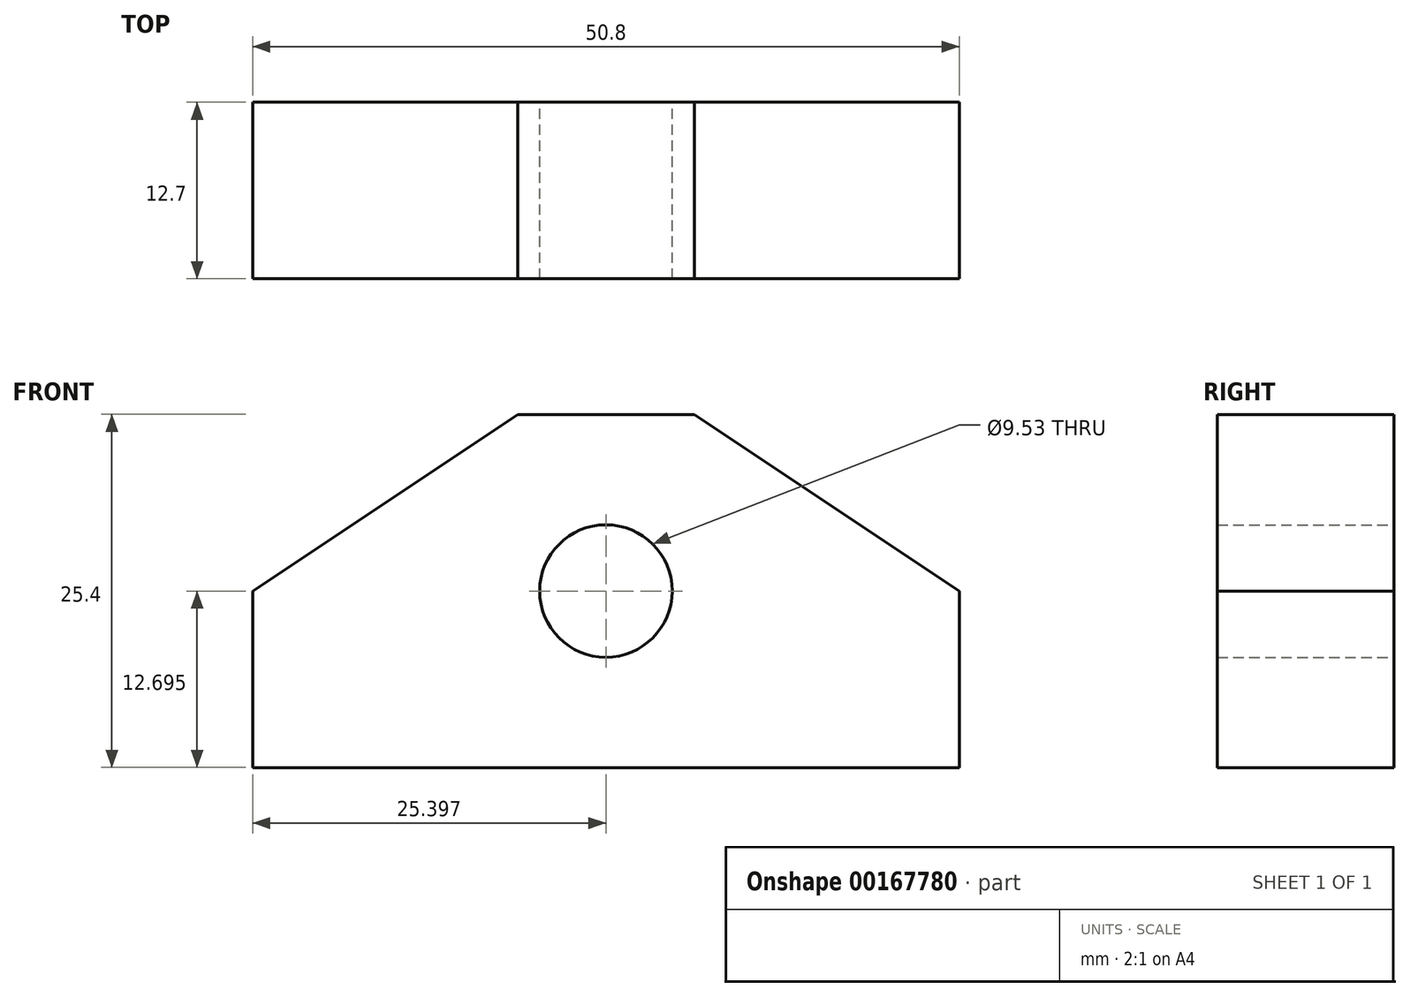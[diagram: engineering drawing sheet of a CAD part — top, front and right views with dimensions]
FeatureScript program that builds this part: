
annotation { "Feature Type Name" : "Feature", "Feature Type Description" : "" }
export const myFeature = defineFeature(function(context is Context, id is Id, definition is map)
    precondition{}
    {
        {
            var Q0;
            Q0=qCreatedBy(makeId("Front.planeOp"),FACE);
            var sketch = newSketch(context, id + "F0", { "sketchPlane" : qUnion([Q0])});
            skLineSegment(sketch, "E0", {"start": v(-38.72, -23.68) * mm, "end": v(12.08, -23.68) * mm});
            skLineSegment(sketch, "E1", {"start": v(12.08, -23.68) * mm, "end": v(12.08, -10.98) * mm});
            skLineSegment(sketch, "E2", {"start": v(12.08, -10.98) * mm, "end": v(-6.97, -10.98) * mm});
            skLineSegment(sketch, "E3", {"start": v(-38.72, -23.68) * mm, "end": v(-38.72, -10.98) * mm});
            skLineSegment(sketch, "E4", {"start": v(-38.72, -10.98) * mm, "end": v(-19.67, -10.98) * mm});
            skCircle(sketch, "E5", {"center": v(-13.32, -10.98) * mm, "radius": 4.76 * mm});
            skLineSegment(sketch, "E6", {"start": v(-19.67, -10.98) * mm, "end": v(-19.67, 1.72) * mm});
            skLineSegment(sketch, "E7", {"start": v(-6.97, -10.98) * mm, "end": v(-6.97, 1.72) * mm});
            skLineSegment(sketch, "E8", {"start": v(-6.97, 1.72) * mm, "end": v(-19.67, 1.72) * mm});
            skLineSegment(sketch, "E9", {"start": v(-19.67, 1.72) * mm, "end": v(-38.72, -10.98) * mm});
            skLineSegment(sketch, "E10", {"start": v(-6.97, 1.72) * mm, "end": v(12.08, -10.98) * mm});
            skSolve(sketch);
        }
        {
            var Q0;
            Q0=makeQuery(id+"F0.imprint","IMPRINT",FACE,{"disambiguationData":[TD([[makeQuery(id+"F0.imprint","IMPRINT",EDGE,{"derivedFrom":sQuery(id+"F0.wireOp",EDGE,"E0")}),1.0]])]});
            var Q1;
            Q1=makeQuery(id+"F0.imprint","IMPRINT",FACE,{"disambiguationData":[TD([[makeQuery(id+"F0.imprint","IMPRINT",EDGE,{"derivedFrom":sQuery(id+"F0.wireOp",EDGE,"E4")}),1.0]])]});
            var Q2;
            Q2=makeQuery(id+"F0.imprint","IMPRINT",FACE,{"disambiguationData":[TD([[makeQuery(id+"F0.imprint","IMPRINT",EDGE,{"derivedFrom":sQuery(id+"F0.wireOp",EDGE,"E2")}),-1.0]])]});
            extrude(context, id + "F1", {"entities" : qUnion([Q0, Q1, Q2]), "depth" : 12.7 * mm});
        }
    });
